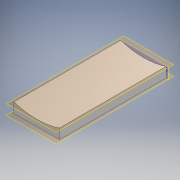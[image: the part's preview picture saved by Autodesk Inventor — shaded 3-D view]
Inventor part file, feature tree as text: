
AUTODESK INVENTOR PART (.ipt)
format: ipt  version: 2018 (Build 220112000, 112)  size: 100,864 bytes
history: native  units: mm
features: plane x2, extrude x1, sketch x1
ambient origin geometry x8: Origin, YZ Plane, XZ Plane, XY Plane, X Axis, Y Axis, Z Axis, Center Point
bodies: Solid1 (feature_tree)
feature tree (4):
  plane  "Work Plane1"
  extrude  "Extrusion1"  Depth=85.0mm
  plane  "Work Plane3"
  sketch  "Sketch1"  dims[d0=-200.0mm d1=85.0mm d2=19.0mm d3=19.0mm d4=135.0mm d5=200.0mm d6=0.0mm d8=19.0mm]
